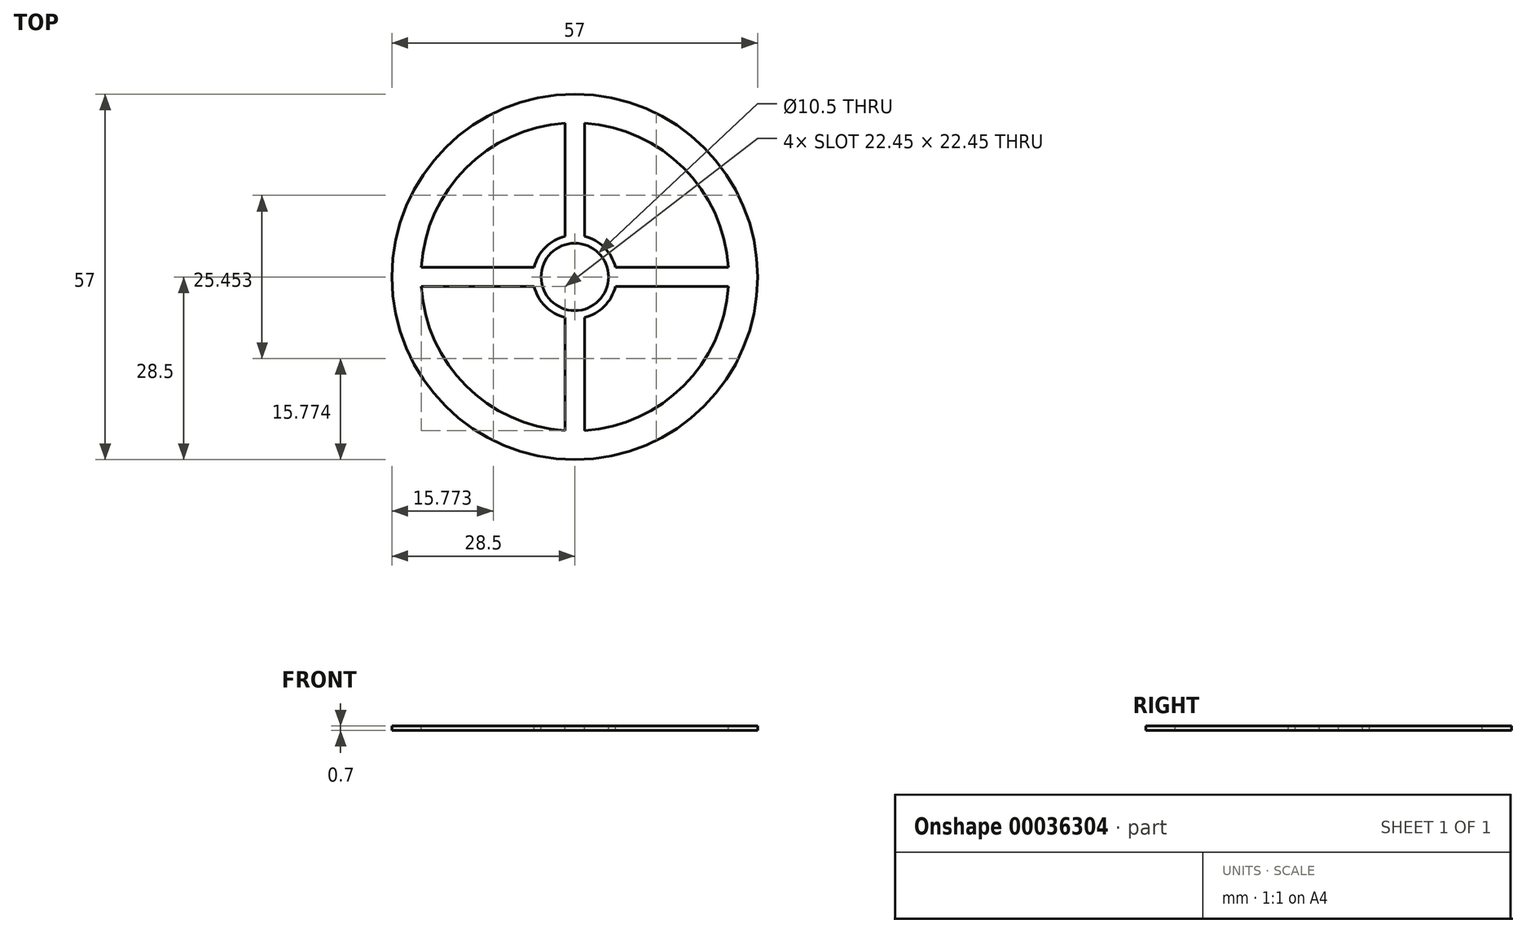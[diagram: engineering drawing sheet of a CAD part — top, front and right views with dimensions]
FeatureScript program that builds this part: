
annotation { "Feature Type Name" : "Feature", "Feature Type Description" : "" }
export const myFeature = defineFeature(function(context is Context, id is Id, definition is map)
    precondition{}
    {
        {
            var Q0;
            Q0=qCreatedBy(makeId("Top.planeOp"),FACE);
            var sketch = newSketch(context, id + "F0", { "sketchPlane" : qUnion([Q0])});
            skCircle(sketch, "E0", {"center": v(0, 0) * mm, "radius": 28.5 * mm});
            skSolve(sketch);
        }
        {
            var Q0;
            Q0=qSketchRegion(id+"F0",true);
            extrude(context, id + "F1", {"entities" : qUnion([Q0]), "depth" : 0.7 * mm});
        }
        {
            var Q0;
            Q0=makeQuery(id+"F1.opExtrude","CAP_FACE",FACE,{"disambiguationData":[OSD([sQuery(id+"F0.wireOp",EDGE,"E0")])],"isStart":false});
            var sketch = newSketch(context, id + "F2", { "sketchPlane" : qUnion([Q0])});
            skCircle(sketch, "E1", {"center": v(0, 0) * mm, "radius": 5.25 * mm});
            skSolve(sketch);
        }
        {
            var Q0;
            Q0=makeQuery(id+"F2.imprint","IMPRINT",FACE,{"disambiguationData":[TD([[makeQuery(id+"F2.imprint","IMPRINT",EDGE,{"derivedFrom":sQuery(id+"F2.wireOp",EDGE,"E1")}),1.0]])]});
            extrude(context, id + "F3", {"entities" : qUnion([Q0]), "operationType" : NewBodyOperationType.REMOVE, "endBound" : BoundingType.UP_TO_NEXT, "oppositeDirection" : true, "depth" : 25 * mm});
        }
        {
            var Q0;
            Q0=makeQuery(id+"F1.opExtrude","CAP_FACE",FACE,{"disambiguationData":[OSD([sQuery(id+"F0.wireOp",EDGE,"E0")])],"isStart":false});
            var sketch = newSketch(context, id + "F4", { "sketchPlane" : qUnion([Q0])});
            skCircle(sketch, "E2", {"center": v(0, 0) * mm, "radius": 24 * mm});
            skCircle(sketch, "E3", {"center": v(0, 0) * mm, "radius": 6.5 * mm});
            skLineSegment(sketch, "E4", {"start": v(0, -6.5) * mm, "end": v(0, -24) * mm, "construction": true});
            skLineSegment(sketch, "E5", {"start": v(-6.5, 0) * mm, "end": v(-24, 0) * mm, "construction": true});
            skLineSegment(sketch, "E6", {"start": v(0, 6.5) * mm, "end": v(0, 24) * mm, "construction": true});
            skLineSegment(sketch, "E7", {"start": v(6.5, 0) * mm, "end": v(24, 0) * mm, "construction": true});
            skLineSegment(sketch, "E8.0", {"start": v(1.5, 6.32) * mm, "end": v(1.5, 23.95) * mm});
            skLineSegment(sketch, "E9.0", {"start": v(-1.5, 6.32) * mm, "end": v(-1.5, 23.95) * mm});
            skLineSegment(sketch, "E10", {"start": v(1.5, -6.32) * mm, "end": v(1.5, -23.95) * mm});
            skLineSegment(sketch, "E11", {"start": v(-1.5, -6.32) * mm, "end": v(-1.5, -23.95) * mm});
            skLineSegment(sketch, "E12.0", {"start": v(6.32, 1.5) * mm, "end": v(23.95, 1.5) * mm});
            skLineSegment(sketch, "E13.0", {"start": v(6.32, -1.5) * mm, "end": v(23.95, -1.5) * mm});
            skLineSegment(sketch, "E14", {"start": v(-6.32, 1.5) * mm, "end": v(-23.95, 1.5) * mm});
            skLineSegment(sketch, "E15", {"start": v(-6.32, -1.5) * mm, "end": v(-23.95, -1.5) * mm});
            skLineSegment(sketch, "E16", {"start": v(-24, -0.3) * mm, "end": v(-28.5, -0.3) * mm, "construction": true});
            skLineSegment(sketch, "E17", {"start": v(24, 0) * mm, "end": v(28.5, 0) * mm, "construction": true});
            skLineSegment(sketch, "E18", {"start": v(0, -24) * mm, "end": v(0, -28.5) * mm, "construction": true});
            skLineSegment(sketch, "E19", {"start": v(0, 24) * mm, "end": v(0, 28.5) * mm, "construction": true});
            skSolve(sketch);
        }
        {
            var Q0;
            {var subQ1=sQuery(id+"F4.wireOp",EDGE,"E9.0");Q0=makeQuery(id+"F4.imprint","IMPRINT",FACE,{"disambiguationData":[TD([[makeQuery(id+"F4.imprint","IMPRINT",EDGE,{"derivedFrom":subQ1}),1.0]])]});}
            var Q1;
            {var subQ1=sQuery(id+"F4.wireOp",EDGE,"E8.0");Q1=makeQuery(id+"F4.imprint","IMPRINT",FACE,{"disambiguationData":[TD([[makeQuery(id+"F4.imprint","IMPRINT",EDGE,{"derivedFrom":subQ1}),-1.0]])]});}
            var Q2;
            {var subQ1=sQuery(id+"F4.wireOp",EDGE,"E10");Q2=makeQuery(id+"F4.imprint","IMPRINT",FACE,{"disambiguationData":[TD([[makeQuery(id+"F4.imprint","IMPRINT",EDGE,{"derivedFrom":subQ1}),1.0]])]});}
            var Q3;
            {var subQ1=sQuery(id+"F4.wireOp",EDGE,"E11");Q3=makeQuery(id+"F4.imprint","IMPRINT",FACE,{"disambiguationData":[TD([[makeQuery(id+"F4.imprint","IMPRINT",EDGE,{"derivedFrom":subQ1}),-1.0]])]});}
            extrude(context, id + "F5", {"entities" : qUnion([Q0, Q1, Q2, Q3]), "operationType" : NewBodyOperationType.REMOVE, "endBound" : BoundingType.UP_TO_NEXT, "oppositeDirection" : true, "depth" : 25 * mm});
        }
    });
